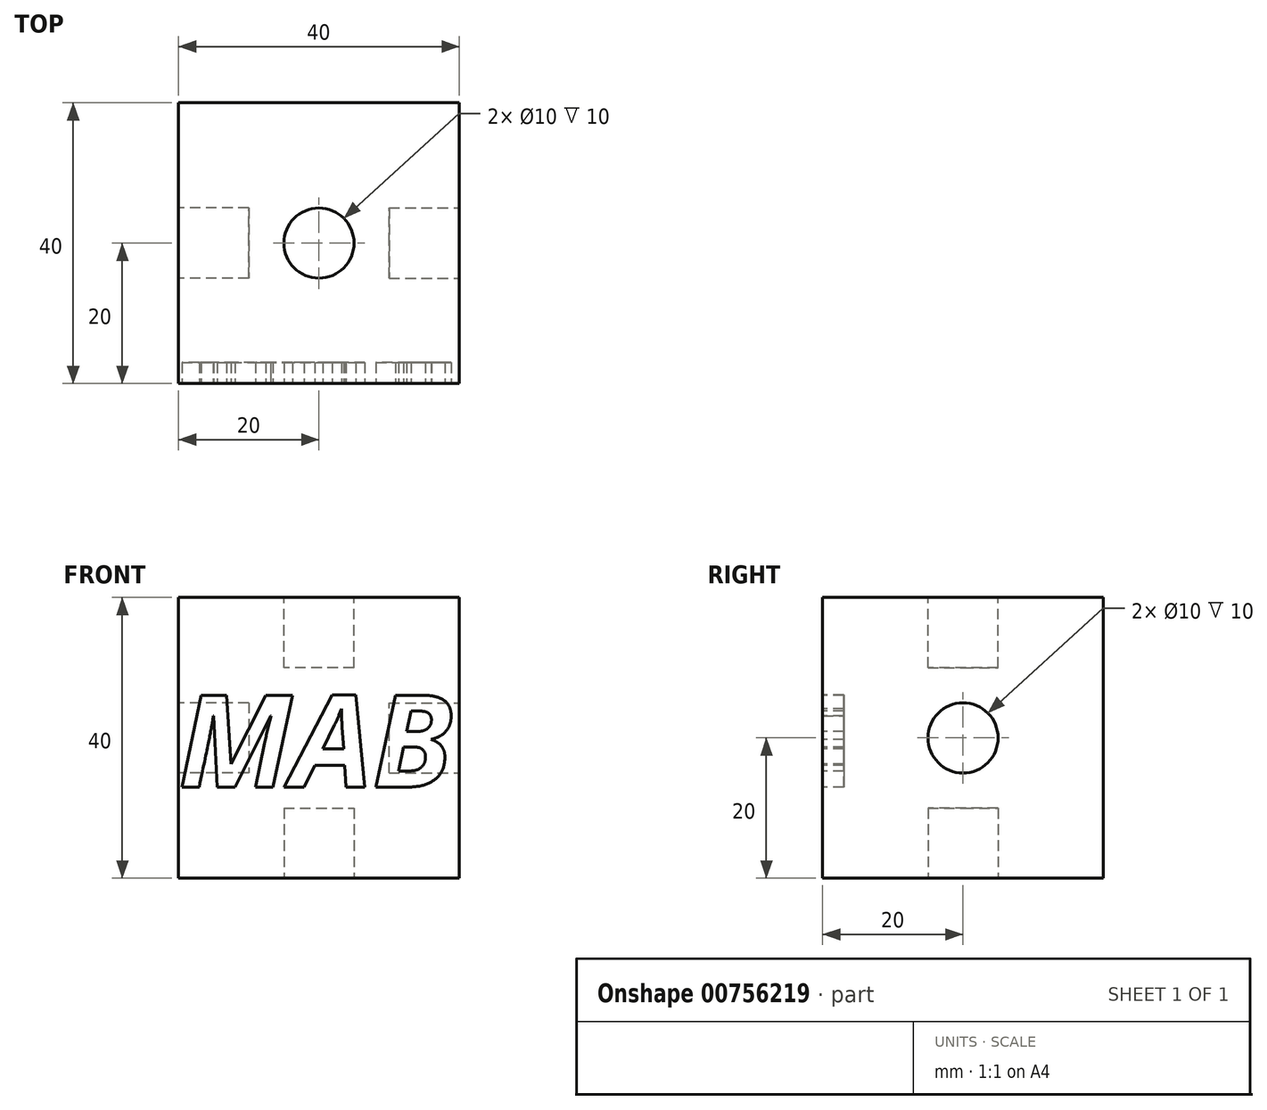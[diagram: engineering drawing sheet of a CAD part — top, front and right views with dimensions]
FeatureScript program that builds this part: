
annotation { "Feature Type Name" : "Feature", "Feature Type Description" : "" }
export const myFeature = defineFeature(function(context is Context, id is Id, definition is map)
    precondition{}
    {
        {
            var Q0;
            Q0=qCreatedBy(makeId("Front.planeOp"),FACE);
            var sketch = newSketch(context, id + "F0", { "sketchPlane" : qUnion([Q0])});
            skLineSegment(sketch, "E0.bottom", {"start": v(-20, 20) * mm, "end": v(20, 20) * mm});
            skLineSegment(sketch, "E0.top", {"start": v(-20, -20) * mm, "end": v(20, -20) * mm});
            skLineSegment(sketch, "E0.left", {"start": v(-20, 20) * mm, "end": v(-20, -20) * mm});
            skLineSegment(sketch, "E0.right", {"start": v(20, 20) * mm, "end": v(20, -20) * mm});
            skSolve(sketch);
        }
        {
            var Q0;
            Q0 = qSketchRegion(id + "F0", true);
            extrude(context, id + "F1", {"entities" : qUnion([Q0]), "depth" : 40 * mm, "offsetDistance" : 25 * mm});
        }
        {
            var Q0;
            Q0=makeQuery(id+"F1.opExtrude","CAP_FACE",FACE,{"disambiguationData":[OSD([sQuery(id+"F0.wireOp",EDGE,"E0.bottom"),sQuery(id+"F0.wireOp",EDGE,"E0.top"),sQuery(id+"F0.wireOp",EDGE,"E0.left"),sQuery(id+"F0.wireOp",EDGE,"E0.right")])],"isStart":false});
            var sketch = newSketch(context, id + "F2", { "sketchPlane" : qUnion([Q0])});
            skText(sketch, "E1", { "text": "MAB", "fontName": "OpenSans-BoldItalic.ttf"});
            const initialGuessF2  = {"E1": [-0.02, -0.007, 1, 0, 0.0132]};
            skSetInitialGuess(sketch, initialGuessF2);
            skSolve(sketch);
        }
        {
            var Q0;
            Q0 = qSketchRegion(id + "F2", true);
            extrude(context, id + "F3", {"entities" : qUnion([Q0]), "operationType" : NewBodyOperationType.REMOVE, "oppositeDirection" : true, "depth" : 3 * mm, "offsetDistance" : 25 * mm});
        }
        {
            var Q0;
            Q0=makeQuery(id+"F1.opExtrude","SWEPT_FACE",FACE,{"disambiguationData":[OSD([sQuery(id+"F0.wireOp",EDGE,"E0.bottom")])]});
            var sketch = newSketch(context, id + "F4", { "sketchPlane" : qUnion([Q0])});
            skCircle(sketch, "E2", {"center": v(0, -20) * mm, "radius": 5 * mm});
            skSolve(sketch);
        }
        {
            var Q0;
            Q0 = qSketchRegion(id + "F4", true);
            extrude(context, id + "F5", {"entities" : qUnion([Q0]), "operationType" : NewBodyOperationType.REMOVE, "oppositeDirection" : true, "depth" : 10 * mm, "offsetDistance" : 25 * mm});
        }
        {
            var Q0;
            Q0=makeQuery(id+"F1.opExtrude","SWEPT_FACE",FACE,{"disambiguationData":[OSD([sQuery(id+"F0.wireOp",EDGE,"E0.right")])]});
            var sketch = newSketch(context, id + "F6", { "sketchPlane" : qUnion([Q0])});
            skCircle(sketch, "E3", {"center": v(-20, 0) * mm, "radius": 5 * mm});
            skSolve(sketch);
        }
        {
            var Q0;
            Q0 = qSketchRegion(id + "F6", true);
            extrude(context, id + "F7", {"entities" : qUnion([Q0]), "operationType" : NewBodyOperationType.REMOVE, "oppositeDirection" : true, "depth" : 10 * mm, "offsetDistance" : 25 * mm});
        }
        {
            var Q0;
            Q0=makeQuery(id+"F1.opExtrude","SWEPT_FACE",FACE,{"disambiguationData":[OSD([sQuery(id+"F0.wireOp",EDGE,"E0.left")])]});
            var sketch = newSketch(context, id + "F8", { "sketchPlane" : qUnion([Q0])});
            skCircle(sketch, "E4", {"center": v(20, 0) * mm, "radius": 5 * mm});
            skSolve(sketch);
        }
        {
            var Q0;
            Q0 = qSketchRegion(id + "F8", true);
            extrude(context, id + "F9", {"entities" : qUnion([Q0]), "operationType" : NewBodyOperationType.REMOVE, "oppositeDirection" : true, "depth" : 10 * mm, "offsetDistance" : 25 * mm});
        }
        {
            var Q0;
            Q0=makeQuery(id+"F1.opExtrude","SWEPT_FACE",FACE,{"disambiguationData":[OSD([sQuery(id+"F0.wireOp",EDGE,"E0.top")])]});
            var sketch = newSketch(context, id + "F10", { "sketchPlane" : qUnion([Q0])});
            skCircle(sketch, "E5", {"center": v(0, 20) * mm, "radius": 5 * mm});
            skSolve(sketch);
        }
        {
            var Q0;
            Q0 = qSketchRegion(id + "F10", true);
            extrude(context, id + "F11", {"entities" : qUnion([Q0]), "operationType" : NewBodyOperationType.REMOVE, "oppositeDirection" : true, "depth" : 10 * mm, "offsetDistance" : 25 * mm});
        }
    });
